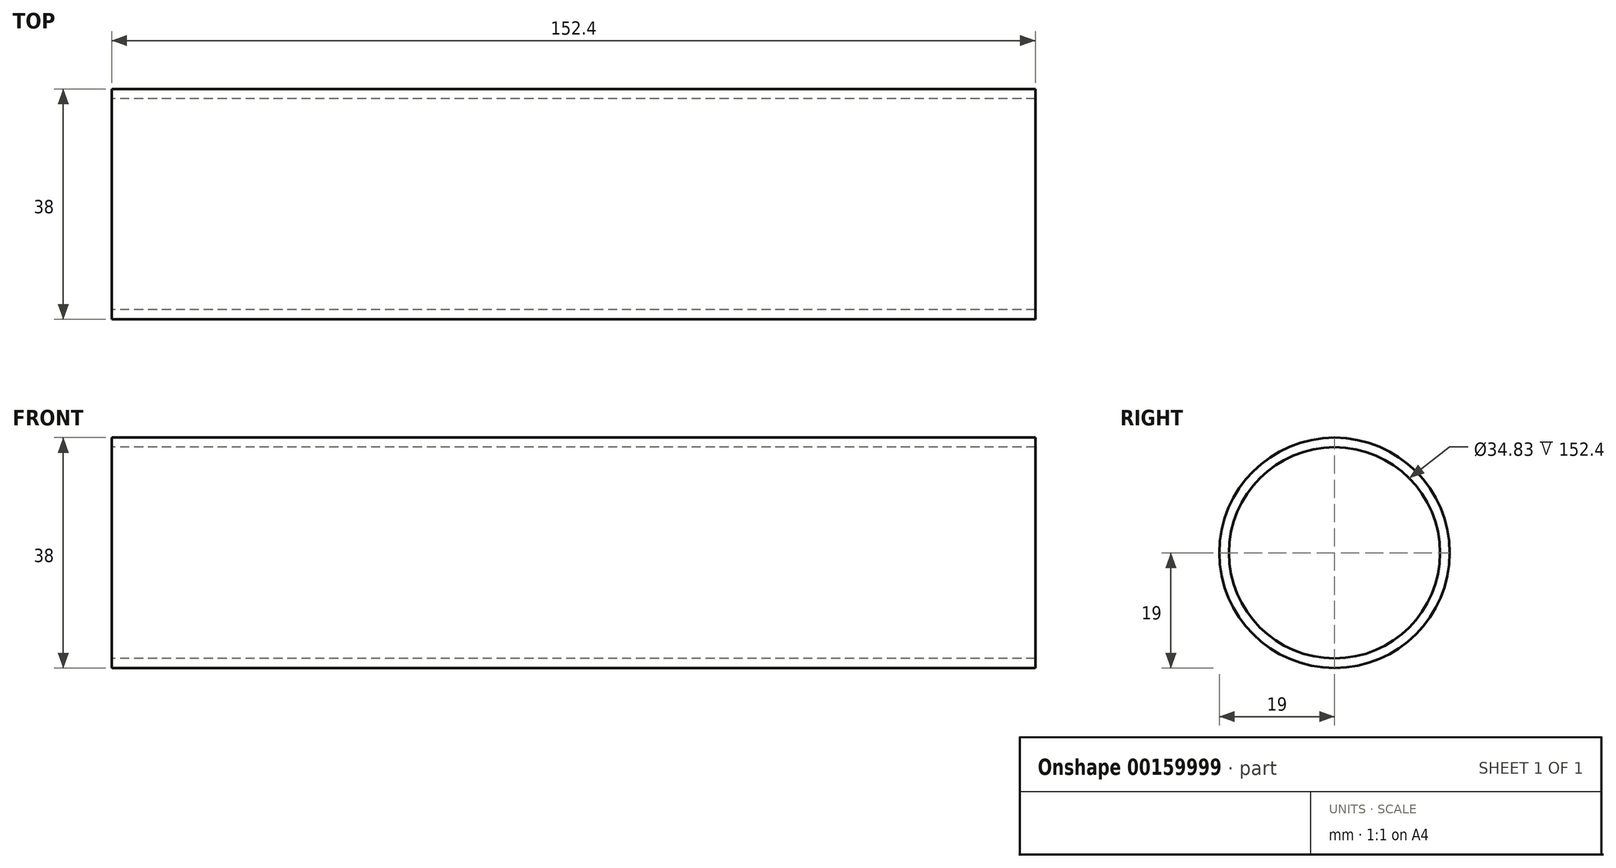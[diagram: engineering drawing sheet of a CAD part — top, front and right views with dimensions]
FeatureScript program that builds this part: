
annotation { "Feature Type Name" : "Feature", "Feature Type Description" : "" }
export const myFeature = defineFeature(function(context is Context, id is Id, definition is map)
    precondition{}
    {
        {
            var Q0;
            Q0=qCreatedBy(makeId("Right.planeOp"),FACE);
            var sketch = newSketch(context, id + "F0", { "sketchPlane" : qUnion([Q0])});
            skCircle(sketch, "E0", {"center": v(0, 0) * mm, "radius": 17.41 * mm});
            skCircle(sketch, "E1", {"center": v(0, 0) * mm, "radius": 19 * mm});
            skSolve(sketch);
        }
        {
            var Q0;
            Q0=makeQuery(id+"F0.imprint","IMPRINT",FACE,{"disambiguationData":[TD([[makeQuery(id+"F0.imprint","IMPRINT",EDGE,{"derivedFrom":sQuery(id+"F0.wireOp",EDGE,"E0")}),-1.0]])]});
            extrude(context, id + "F1", {"entities" : qUnion([Q0]), "depth" : 152.4 * mm});
        }
    });
